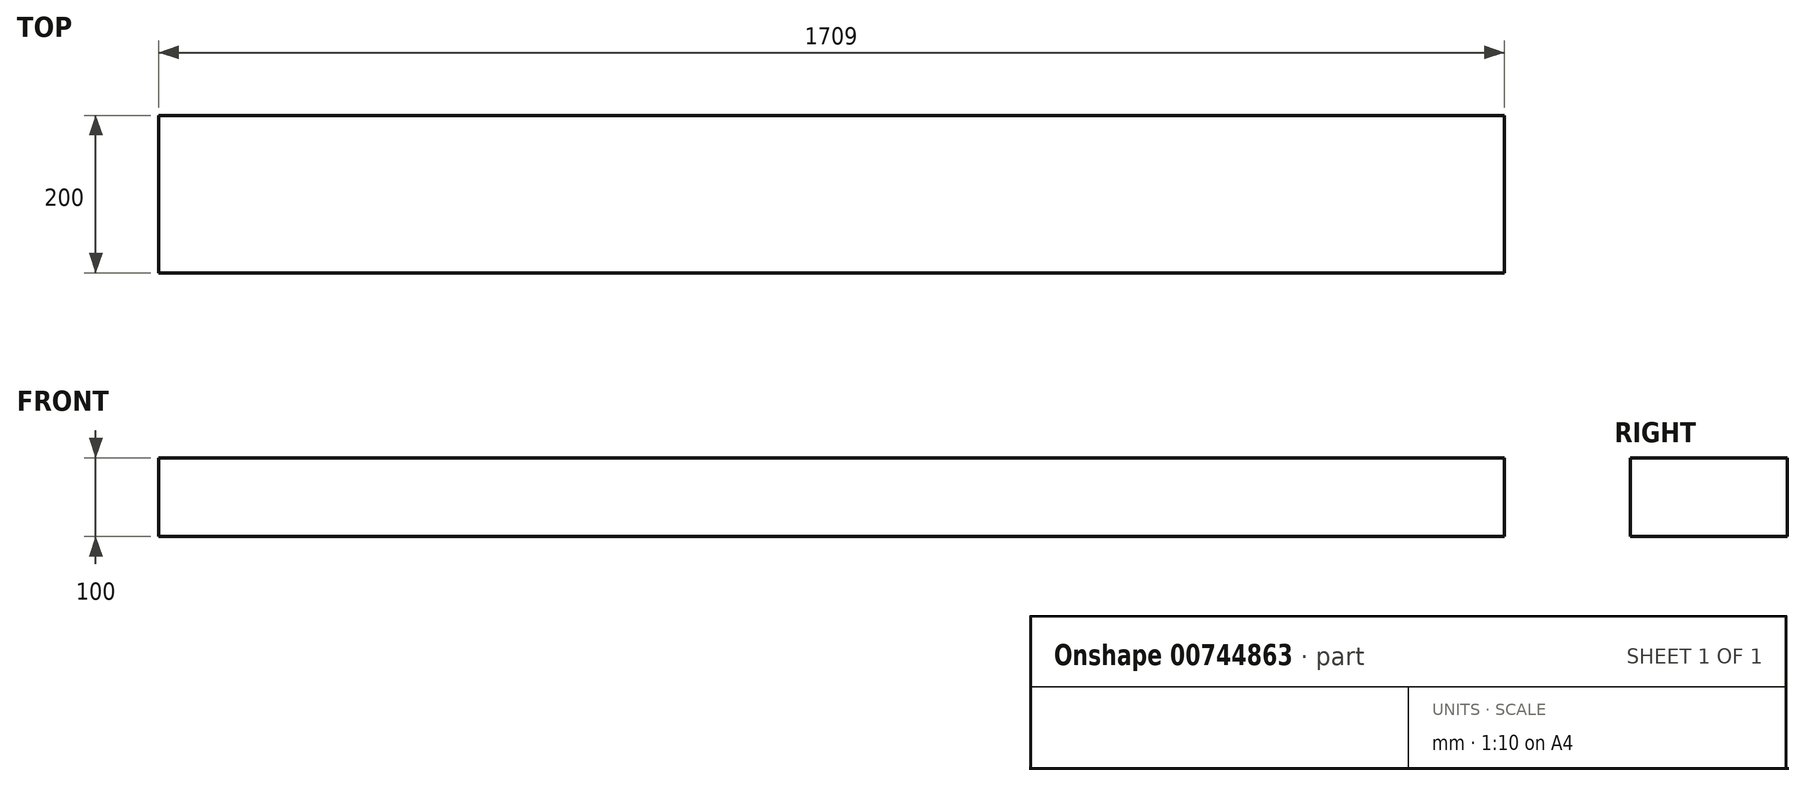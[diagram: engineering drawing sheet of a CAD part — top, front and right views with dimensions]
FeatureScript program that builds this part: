
annotation { "Feature Type Name" : "Feature", "Feature Type Description" : "" }
export const myFeature = defineFeature(function(context is Context, id is Id, definition is map)
    precondition{}
    {
        {
            var Q0;
            Q0=qCreatedBy(makeId("Right.planeOp"),FACE);
            var sketch = newSketch(context, id + "F0", { "sketchPlane" : qUnion([Q0])});
            skLineSegment(sketch, "E0.bottom", {"start": v(0, 0) * mm, "end": v(-200, 0) * mm});
            skLineSegment(sketch, "E0.top", {"start": v(0, 100) * mm, "end": v(-200, 100) * mm});
            skLineSegment(sketch, "E0.left", {"start": v(0, 0) * mm, "end": v(0, 100) * mm});
            skLineSegment(sketch, "E0.right", {"start": v(-200, 0) * mm, "end": v(-200, 100) * mm});
            skSolve(sketch);
        }
        {
            var Q0;
            Q0=makeQuery(id+"F0.imprint","IMPRINT",FACE,{"disambiguationData":[TD([[makeQuery(id+"F0.imprint","IMPRINT",EDGE,{"derivedFrom":sQuery(id+"F0.wireOp",EDGE,"E0.bottom")}),-1.0]])]});
            extrude(context, id + "F1", {"entities" : qUnion([Q0]), "flatOperationType" : FlatOperationType.REMOVE, "depth" : (1800 - 91) * mm, "offsetDistance" : 25 * mm, "domain" : OperationDomain.MODEL});
        }
    });
